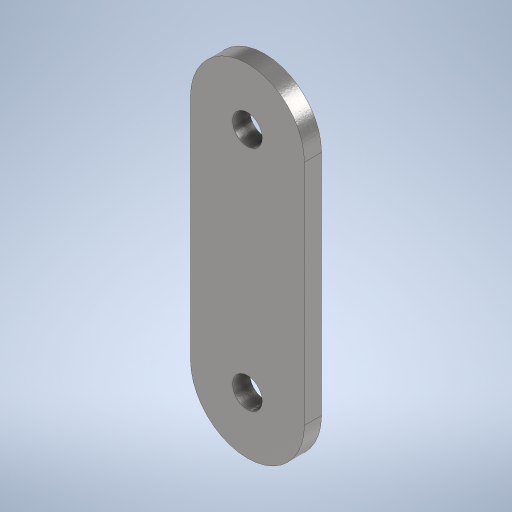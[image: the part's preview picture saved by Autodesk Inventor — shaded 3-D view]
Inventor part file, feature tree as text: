
AUTODESK INVENTOR PART (.ipt)
format: ipt  version: 2024.2 (Build 282272000, 272)  size: 238,080 bytes
history: native  units: mm
features: extrude x1, sketch x1
ambient origin geometry x8: Origin, YZ Plane, XZ Plane, XY Plane, X Axis, Y Axis, Z Axis, Center Point
bodies: Solid1 (feature_tree)
feature tree (2):
  extrude  "Extrusion1"  Depth=20.0mm
  sketch  "Sketch1"  dims[d8=3.0mm d9=0.0mm d15=20.0mm d16=20.0mm d17=40.0mm d18=10.0mm d19=5.2mm]
